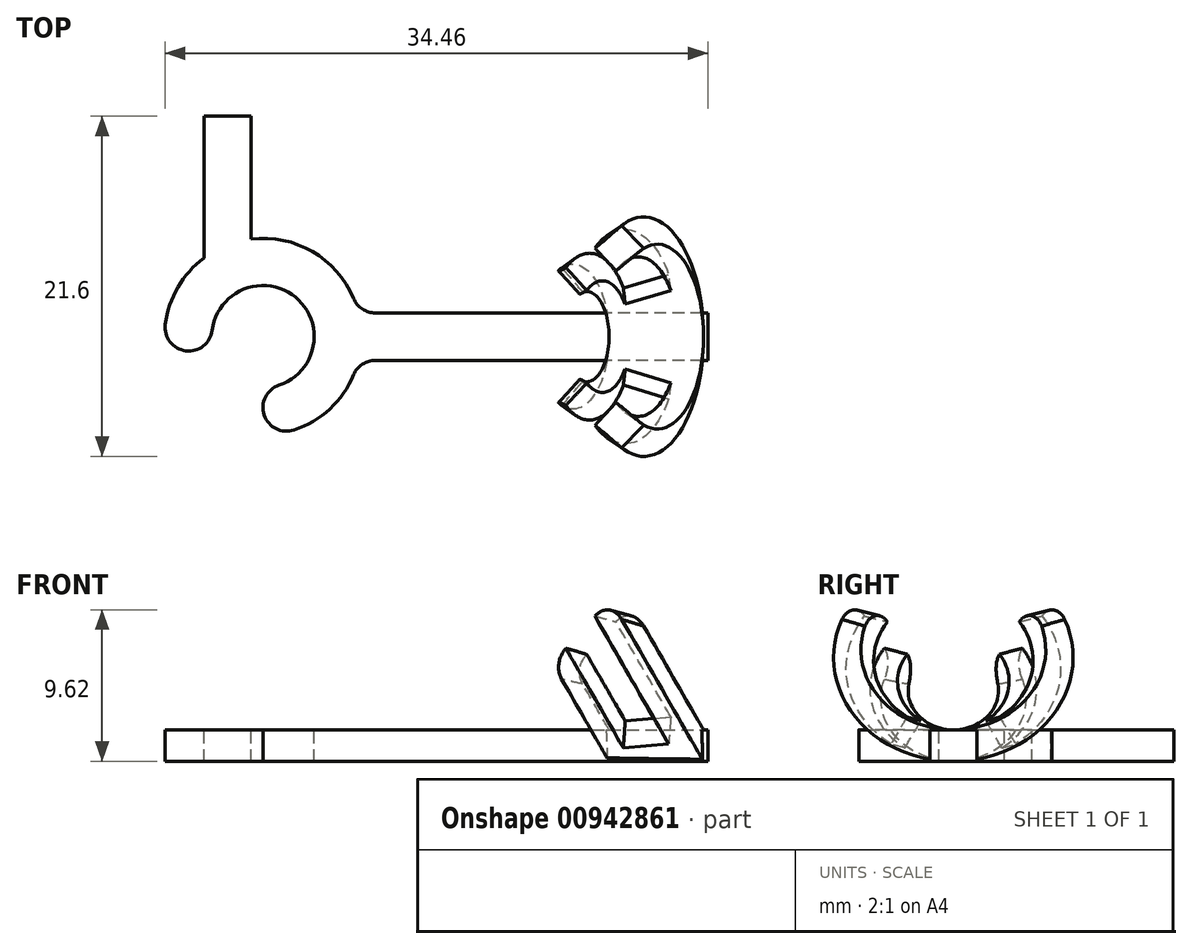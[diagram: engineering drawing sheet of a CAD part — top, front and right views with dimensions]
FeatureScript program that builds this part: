
annotation { "Feature Type Name" : "Feature", "Feature Type Description" : "" }
export const myFeature = defineFeature(function(context is Context, id is Id, definition is map)
    precondition{}
    {
        {
            var Q0;
            Q0=qCreatedBy(makeId("Top.planeOp"),FACE);
            var sketch = newSketch(context, id + "F0", { "sketchPlane" : qUnion([Q0])});
            skLineSegment(sketch, "E0.bottom", {"start": v(-25, 1.5) * mm, "end": v(0, 1.5) * mm});
            skLineSegment(sketch, "E0.top", {"start": v(-25, -1.5) * mm, "end": v(0, -1.5) * mm});
            skLineSegment(sketch, "E0.left", {"start": v(-25, 1.5) * mm, "end": v(-25, -1.5) * mm});
            skLineSegment(sketch, "E0.right", {"start": v(0, 1.5) * mm, "end": v(0, -1.5) * mm});
            skLineSegment(sketch, "E1.bottom", {"start": v(-32, 4.5) * mm, "end": v(-29, 4.5) * mm});
            skLineSegment(sketch, "E1.top", {"start": v(-32, 14) * mm, "end": v(-29, 14) * mm});
            skLineSegment(sketch, "E1.left", {"start": v(-32, 4.5) * mm, "end": v(-32, 14) * mm});
            skLineSegment(sketch, "E1.right", {"start": v(-29, 4.5) * mm, "end": v(-29, 14) * mm});
            skSolve(sketch);
        }
        {
            var Q0;
            Q0=makeQuery(id+"F0.imprint","IMPRINT",FACE,{"disambiguationData":[TD([[makeQuery(id+"F0.imprint","IMPRINT",EDGE,{"derivedFrom":sQuery(id+"F0.wireOp",EDGE,"E1.bottom")}),1.0]])]});
            extrude(context, id + "F1", {"entities" : qUnion([Q0]), "depth" : 2 * mm});
        }
        {
            var Q0;
            Q0=makeQuery(id+"F0.imprint","IMPRINT",FACE,{"disambiguationData":[TD([[makeQuery(id+"F0.imprint","IMPRINT",EDGE,{"derivedFrom":sQuery(id+"F0.wireOp",EDGE,"E0.bottom")}),-1.0]])]});
            extrude(context, id + "F2", {"entities" : qUnion([Q0]), "depth" : 2 * mm});
        }
        {
            var Q0;
            Q0=qCreatedBy(makeId("Front.planeOp"),FACE);
            var sketch = newSketch(context, id + "F3", { "sketchPlane" : qUnion([Q0])});
            skLineSegment(sketch, "E2.bottom", {"start": v(-25, 0) * mm, "end": v(-22, 0) * mm});
            skLineSegment(sketch, "E2.top", {"start": v(-25, 2) * mm, "end": v(-22, 2) * mm});
            skLineSegment(sketch, "E2.left", {"start": v(-25, 0) * mm, "end": v(-25, 2) * mm});
            skLineSegment(sketch, "E2.right", {"start": v(-22, 0) * mm, "end": v(-22, 2) * mm});
            skLineSegment(sketch, "E3", {"start": v(-28.25, 3.51) * mm, "end": v(-28.25, -2.02) * mm});
            skSolve(sketch);
        }
        {
            var Q0;
            Q0=qSketchRegion(id+"F3",true);
            var Q1;
            Q1=sQuery(id+"F3.wireOp",EDGE,"E3");
            revolve(context, id + "F4", {"operationType" : NewBodyOperationType.ADD, "entities" : qUnion([Q0]), "axis" : qUnion([Q1]), "revolveType" : RevolveType.TWO_DIRECTIONS, "angle" : 90 * degree, "angleBack" : 168.74 * degree});
        }
        {
            var Q0;
            Q0=qCreatedBy(makeId("Front.planeOp"),FACE);
            var sketch = newSketch(context, id + "F5", { "sketchPlane" : qUnion([Q0])});
            skLineSegment(sketch, "E4.bottom", {"start": v(-6.27, 0) * mm, "end": v(-0.27, 0) * mm});
            skLineSegment(sketch, "E4.top", {"start": v(-6.27, 2) * mm, "end": v(-0.27, 2) * mm});
            skLineSegment(sketch, "E4.left", {"start": v(-6.27, 0) * mm, "end": v(-6.27, 2) * mm});
            skLineSegment(sketch, "E4.right", {"start": v(-0.27, 0) * mm, "end": v(-0.27, 2) * mm});
            skLineSegment(sketch, "E5", {"start": v(-7.85, 4.4) * mm, "end": v(0.08, 8.98) * mm});
            skSolve(sketch);
        }
        {
            var Q0;
            Q0=qSketchRegion(id+"F5",true);
            var Q1;
            Q1=sQuery(id+"F5.wireOp",EDGE,"E5");
            revolve(context, id + "F6", {"operationType" : NewBodyOperationType.ADD, "entities" : qUnion([Q0]), "axis" : qUnion([Q1]), "revolveType" : RevolveType.SYMMETRIC, "angle" : 248.45 * degree});
        }
        {
            var Q0;
            Q0=makeQuery(id+"F6.opRevolve","CAP_EDGE",EDGE,{"disambiguationData":[OSD([sQuery(id+"F5.wireOp",EDGE,"E4.left")])],"isStart":false});
            var Q1;
            Q1=makeQuery(id+"F6.opRevolve","CAP_EDGE",EDGE,{"disambiguationData":[OSD([sQuery(id+"F5.wireOp",EDGE,"E4.right")])],"isStart":false});
            var Q2;
            Q2=makeQuery(id+"F6.opRevolve","CAP_EDGE",EDGE,{"disambiguationData":[OSD([sQuery(id+"F5.wireOp",EDGE,"E4.left")])],"isStart":true});
            var Q3;
            Q3=makeQuery(id+"F6.opRevolve","CAP_EDGE",EDGE,{"disambiguationData":[OSD([sQuery(id+"F5.wireOp",EDGE,"E4.right")])],"isStart":true});
            var Q4;
            Q4=makeQuery(id+"F4.boolean.opBoolean","INTERSECT",EDGE,{"derivedFrom":[makeQuery(id+"F2.opExtrude","SWEPT_FACE",FACE,{"disambiguationData":[OSD([sQuery(id+"F0.wireOp",EDGE,"E0.top")])]}),makeQuery(id+"F4.opRevolve","SWEPT_FACE",FACE,{"disambiguationData":[OSD([sQuery(id+"F3.wireOp",EDGE,"E2.right")])]})]});
            var Q5;
            Q5=makeQuery(id+"F4.opRevolve","CAP_EDGE",EDGE,{"disambiguationData":[OSD([sQuery(id+"F3.wireOp",EDGE,"E2.right")])],"isStart":false});
            var Q6;
            Q6=makeQuery(id+"F4.opRevolve","CAP_EDGE",EDGE,{"disambiguationData":[OSD([sQuery(id+"F3.wireOp",EDGE,"E2.left")])],"isStart":false});
            var Q7;
            Q7=makeQuery(id+"F4.opRevolve","CAP_EDGE",EDGE,{"disambiguationData":[OSD([sQuery(id+"F3.wireOp",EDGE,"E2.right")])],"isStart":true});
            var Q8;
            Q8=makeQuery(id+"F4.opRevolve","CAP_EDGE",EDGE,{"disambiguationData":[OSD([sQuery(id+"F3.wireOp",EDGE,"E2.left")])],"isStart":true});
            var Q9;
            Q9=makeQuery(id+"F4.boolean.opBoolean","INTERSECT",EDGE,{"derivedFrom":[makeQuery(id+"F2.opExtrude","SWEPT_FACE",FACE,{"disambiguationData":[OSD([sQuery(id+"F0.wireOp",EDGE,"E0.bottom")])]}),makeQuery(id+"F4.opRevolve","SWEPT_FACE",FACE,{"disambiguationData":[OSD([sQuery(id+"F3.wireOp",EDGE,"E2.right")])]})]});
            fillet(context, id + "F7", {"entities" : qUnion([Q0, Q1, Q2, Q3, Q4, Q5, Q6, Q7, Q8, Q9]), "radius" : 1.5 * mm, "tangentPropagation" : true, "allowEdgeOverflow" : false});
        }
        {
            var Q0;
            Q0=makeQuery(id+"F6.opRevolve","CAP_FACE",FACE,{"disambiguationData":[OSD([sQuery(id+"F5.wireOp",EDGE,"E4.bottom"),sQuery(id+"F5.wireOp",EDGE,"E4.top"),sQuery(id+"F5.wireOp",EDGE,"E4.left"),sQuery(id+"F5.wireOp",EDGE,"E4.right")])],"isStart":false});
            var Q1;
            Q1=makeQuery(id+"F6.opRevolve","CAP_FACE",FACE,{"disambiguationData":[OSD([sQuery(id+"F5.wireOp",EDGE,"E4.bottom"),sQuery(id+"F5.wireOp",EDGE,"E4.top"),sQuery(id+"F5.wireOp",EDGE,"E4.left"),sQuery(id+"F5.wireOp",EDGE,"E4.right")])],"isStart":true});
            var Q2;
            Q2=sQuery(id+"F5.wireOp",EDGE,"E5");
            revolve(context, id + "F8", {"operationType" : NewBodyOperationType.REMOVE, "entities" : qUnion([Q0, Q1]), "axis" : qUnion([Q2]), "revolveType" : RevolveType.SYMMETRIC, "oppositeDirection" : true, "angle" : 177.46 * degree});
        }
    });
